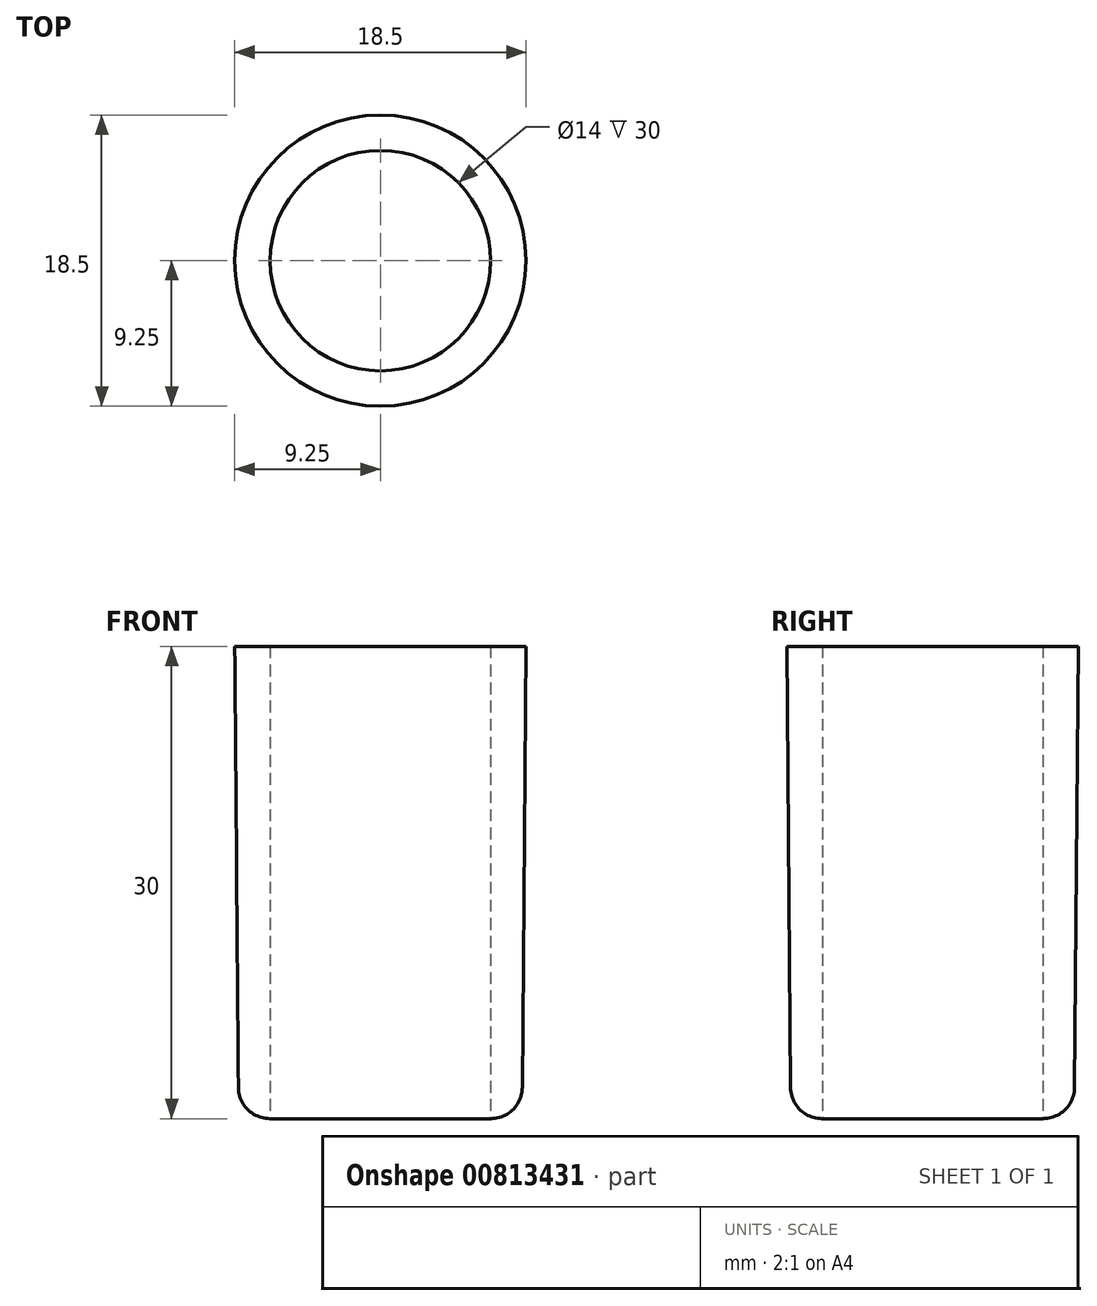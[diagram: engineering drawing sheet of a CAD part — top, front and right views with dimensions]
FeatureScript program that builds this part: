
annotation { "Feature Type Name" : "Feature", "Feature Type Description" : "" }
export const myFeature = defineFeature(function(context is Context, id is Id, definition is map)
    precondition{}
    {
        {
            var Q0;
            Q0=qCreatedBy(makeId("Front.planeOp"),FACE);
            var sketch = newSketch(context, id + "F0", { "sketchPlane" : qUnion([Q0])});
            skLineSegment(sketch, "E0", {"start": v(-7, 0) * mm, "end": v(-7, 30) * mm});
            skLineSegment(sketch, "E1", {"start": v(-7, 30) * mm, "end": v(-9.25, 30) * mm});
            skLineSegment(sketch, "E2", {"start": v(-9.25, 30) * mm, "end": v(-9, 0) * mm});
            skLineSegment(sketch, "E3", {"start": v(-9, 0) * mm, "end": v(-7, 0) * mm});
            skLineSegment(sketch, "E4", {"start": v(0, 0) * mm, "end": v(0, 30) * mm, "construction": true});
            skSolve(sketch);
        }
        {
            var Q0;
            Q0=makeQuery(id+"F0.imprint","IMPRINT",FACE,{"disambiguationData":[TD([[makeQuery(id+"F0.imprint","IMPRINT",EDGE,{"derivedFrom":sQuery(id+"F0.wireOp",EDGE,"E0")}),1.0]])]});
            var Q1;
            Q1=sQuery(id+"F0.wireOp",EDGE,"E4");
            revolve(context, id + "F1", {"surfaceOperationType" : NewSurfaceOperationType.NEW, "entities" : qUnion([Q0]), "axis" : qUnion([Q1]), "revolveType" : RevolveType.FULL});
        }
        {
            var Q0;
            Q0=makeQuery(id+"F1.opRevolve","SWEPT_EDGE",EDGE,{"disambiguationData":[OSD([sQuery(id+"F0.wireOp",EDGE,"E2"),sQuery(id+"F0.wireOp",EDGE,"E3")])]});
            fillet(context, id + "F2", {"entities" : qUnion([Q0]), "tangentPropagation" : true, "radius" : 2 * mm, "defaultsChanged" : true, "vertexSettings" : [], "allowEdgeOverflow" : false});
        }
    });
